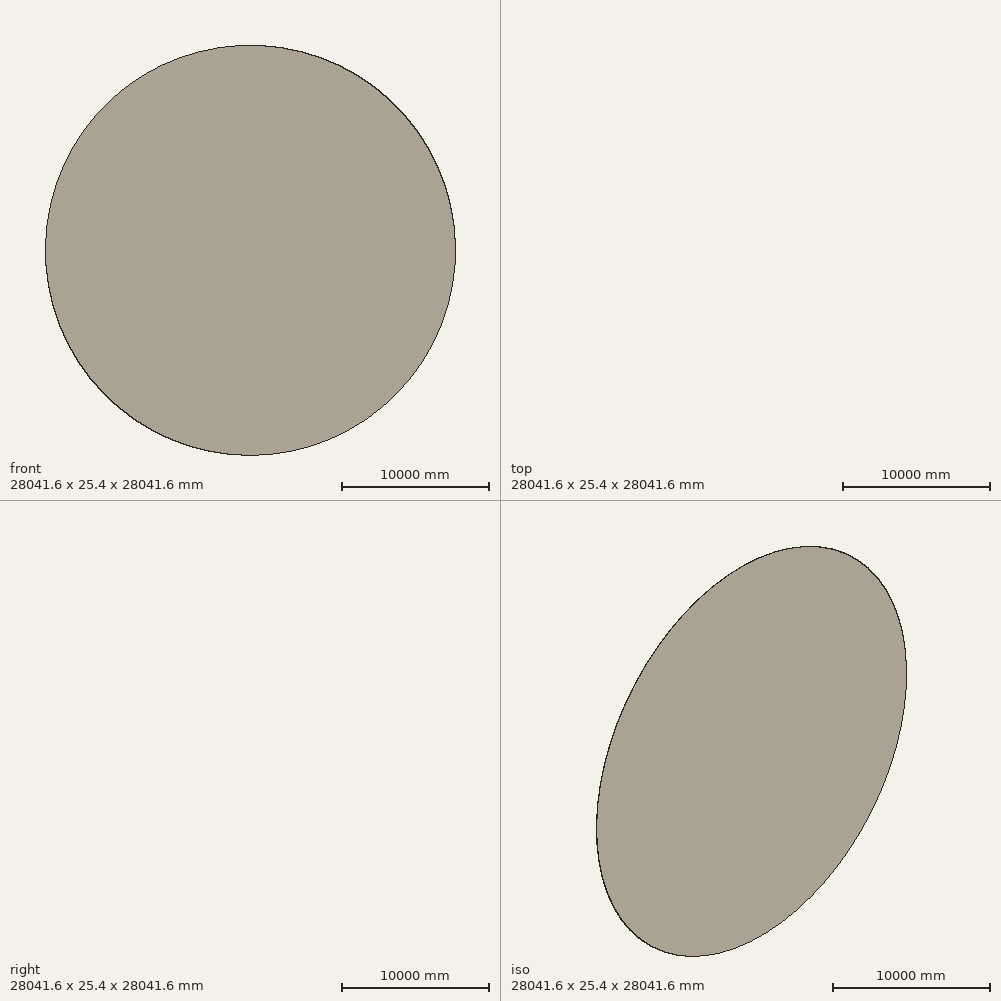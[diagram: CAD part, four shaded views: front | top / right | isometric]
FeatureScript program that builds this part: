
annotation { "Feature Type Name" : "Feature", "Feature Type Description" : "" }
export const myFeature = defineFeature(function(context is Context, id is Id, definition is map)
    precondition{}
    {
        {
            var Q0;
            Q0=qCreatedBy(makeId("Front.planeOp"),FACE);
            var sketch = newSketch(context, id + "F0", { "sketchPlane" : qUnion([Q0])});
            skCircle(sketch, "E0", {"center": v(0, 0) * mm, "radius": 14020.8 * mm});
            skCircle(sketch, "E1", {"center": v(0, 0) * mm, "radius": 13258.8 * mm});
            skSolve(sketch);
        }
        {
            var Q0;
            Q0=makeQuery(id+"F0.imprint","IMPRINT",FACE,{"disambiguationData":[TD([[makeQuery(id+"F0.imprint","IMPRINT",EDGE,{"derivedFrom":sQuery(id+"F0.wireOp",EDGE,"E1")}),1.0]])]});
            var Q1;
            Q1=makeQuery(id+"F0.imprint","IMPRINT",FACE,{"disambiguationData":[TD([[makeQuery(id+"F0.imprint","IMPRINT",EDGE,{"derivedFrom":sQuery(id+"F0.wireOp",EDGE,"E0")}),1.0]])]});
            extrude(context, id + "F1", {"entities" : qUnion([Q0, Q1]), "depth" : 25.4 * mm, "offsetDistance" : 25.4 * mm});
        }
    });
